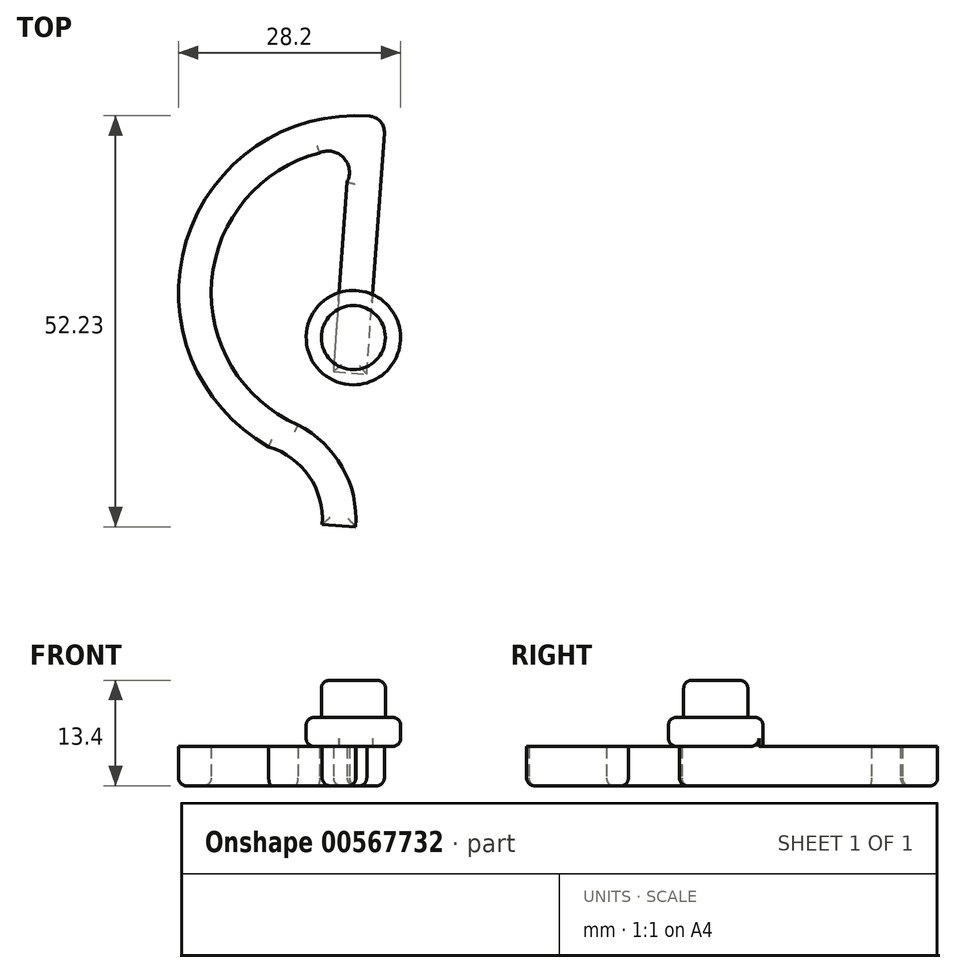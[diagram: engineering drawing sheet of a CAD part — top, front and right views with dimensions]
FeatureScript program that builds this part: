
annotation { "Feature Type Name" : "Feature", "Feature Type Description" : "" }
export const myFeature = defineFeature(function(context is Context, id is Id, definition is map)
    precondition{}
    {
        {
            var Q0;
            Q0=qCreatedBy(makeId("Front.planeOp"),FACE);
            var sketch = newSketch(context, id + "F0", { "sketchPlane" : qUnion([Q0])});
            skEllipticalArc(sketch, "E0", {});
            skArc(sketch, "E1", {"start": v(32.14, -13.74) * mm, "mid": v(46.1, 8.58) * mm, "end": v(25.17, 24.54) * mm});
            skArc(sketch, "E2.filletArc", {"start": v(23.1, 27.15) * mm, "mid": v(23.43, 25.29) * mm, "end": v(25.17, 24.54) * mm});
            skPoint(sketch, "E3.visualSharp", {"position": v(28.3, -14.4) * mm});
            skArc(sketch, "E3.filletArc", {"start": v(32.14, -13.74) * mm, "mid": v(30.7, -15.37) * mm, "end": v(31.6, -17.35) * mm});
            skArc(sketch, "E4", {"start": v(-52.78, 36.46) * mm, "mid": v(-76.5, 19.2) * mm, "end": v(-62.96, -6.82) * mm});
            skLineSegment(sketch, "E5", {"start": v(-55.53, 30.2) * mm, "end": v(-57.43, 4.02) * mm});
            skLineSegment(sketch, "E6", {"start": v(-58.84, -15.39) * mm, "end": v(-54.59, -15.7) * mm});
            skArc(sketch, "E7", {"start": v(-58.18, 32.03) * mm, "mid": v(-72.83, 16.02) * mm, "end": v(-61.94, -2.74) * mm});
            skLineSegment(sketch, "E8", {"start": v(-57.43, 4.02) * mm, "end": v(-53.18, 3.72) * mm});
            skLineSegment(sketch, "E9.trimOffspring", {"start": v(-53.18, 3.72) * mm, "end": v(-50.95, 34.32) * mm});
            skArc(sketch, "E10", {"start": v(-55.68, 28.12) * mm, "mid": v(-56.12, 31.19) * mm, "end": v(-59.16, 31.8) * mm});
            skArc(sketch, "E11", {"start": v(-58.84, -15.39) * mm, "mid": v(-60.5, -9.27) * mm, "end": v(-65.63, -5.54) * mm});
            skArc(sketch, "E12", {"start": v(-54.59, -15.7) * mm, "mid": v(-56.51, -7.74) * mm, "end": v(-62.7, -2.39) * mm});
            skPoint(sketch, "E13.visualSharp", {"position": v(-50.81, 36.21) * mm});
            skArc(sketch, "E13.filletArc", {"start": v(-50.95, 34.32) * mm, "mid": v(-51.43, 35.77) * mm, "end": v(-52.78, 36.46) * mm});
            const initialGuessF0  = {"E0": [0.03683771193027496, 0.011276849545538425, 0, -1, 0.03025954682379961, 0.01614231554877723, 5.952785884912911, 4.160081685940753]};
            skSetInitialGuess(sketch, initialGuessF0);
            skSolve(sketch);
        }
        {
            var Q0;
            {var subQ15=sQuery(id+"F0.wireOp",EDGE,"E6");Q0=makeQuery(id+"F0.imprint","IMPRINT",FACE,{"disambiguationData":[TD([[makeQuery(id+"F0.imprint","IMPRINT",EDGE,{"derivedFrom":subQ15}),1.0]])]});}
            extrude(context, id + "F1", {"entities" : qUnion([Q0]), "depth" : 5 * mm, "offsetDistance" : 25 * mm});
        }
        {
            var Q0;
            Q0=makeQuery(id+"F1.opExtrude","CAP_FACE",FACE,{"disambiguationData":[OSD([sQuery(id+"F0.wireOp",EDGE,"E4"),sQuery(id+"F0.wireOp",EDGE,"E5"),sQuery(id+"F0.wireOp",EDGE,"E6"),sQuery(id+"F0.wireOp",EDGE,"E7"),sQuery(id+"F0.wireOp",EDGE,"E8"),sQuery(id+"F0.wireOp",EDGE,"E9.trimOffspring"),sQuery(id+"F0.wireOp",EDGE,"E10"),sQuery(id+"F0.wireOp",EDGE,"E11"),sQuery(id+"F0.wireOp",EDGE,"E12")])],"isStart":false});
            var sketch = newSketch(context, id + "F2", { "sketchPlane" : qUnion([Q0])});
            skCircle(sketch, "E14", {"center": v(-54.88, 8.34) * mm, "radius": 6 * mm});
            skSolve(sketch);
        }
        {
            var Q0;
            {var subQ5=makeQuery(id+"F1.opExtrude","CAP_EDGE",EDGE,{"disambiguationData":[OSD([sQuery(id+"F0.wireOp",EDGE,"E8")])],"isStart":false});Q0=makeQuery(id+"F2.imprint","IMPRINT",FACE,{"disambiguationData":[TD([[makeQuery(id+"F2.imprint","IMPRINT",EDGE,{"derivedFrom":subQ5}),-1.0]])]});}
            var Q1;
            {var subQ5=makeQuery(id+"F1.opExtrude","CAP_EDGE",EDGE,{"disambiguationData":[OSD([sQuery(id+"F0.wireOp",EDGE,"E8")])],"isStart":false});Q1=makeQuery(id+"F2.imprint","IMPRINT",FACE,{"disambiguationData":[TD([[makeQuery(id+"F2.imprint","IMPRINT",EDGE,{"derivedFrom":subQ5}),1.0]])]});}
            extrude(context, id + "F3", {"entities" : qUnion([Q0, Q1]), "operationType" : NewBodyOperationType.ADD, "depth" : 3.7 * mm, "offsetDistance" : 25 * mm});
        }
        {
            var Q0;
            Q0=makeQuery(id+"F3.opExtrude","CAP_FACE",FACE,{"disambiguationData":[OSD([sQuery(id+"F2.wireOp",EDGE,"E14")])],"isStart":false});
            var sketch = newSketch(context, id + "F4", { "sketchPlane" : qUnion([Q0])});
            skCircle(sketch, "E15", {"center": v(-54.88, 8.34) * mm, "radius": 4.07 * mm});
            skSolve(sketch);
        }
        {
            var Q0;
            Q0=makeQuery(id+"F4.imprint","IMPRINT",FACE,{"disambiguationData":[TD([[makeQuery(id+"F4.imprint","IMPRINT",EDGE,{"derivedFrom":sQuery(id+"F4.wireOp",EDGE,"E15")}),1.0]])]});
            extrude(context, id + "F5", {"entities" : qUnion([Q0]), "operationType" : NewBodyOperationType.ADD, "depth" : 4.7 * mm, "offsetDistance" : 25 * mm});
        }
        {
            var Q0;
            Q0=makeQuery(id+"F5.opExtrude","CAP_EDGE",EDGE,{"disambiguationData":[OSD([sQuery(id+"F4.wireOp",EDGE,"E15")])],"isStart":false});
            fillet(context, id + "F6", {"entities" : qUnion([Q0]), "radius" : 1 * mm, "tangentPropagation" : true, "allowEdgeOverflow" : false});
        }
        {
            var Q0;
            Q0=makeQuery(id+"F3.opExtrude","CAP_EDGE",EDGE,{"disambiguationData":[OSD([sQuery(id+"F2.wireOp",EDGE,"E14")])],"isStart":false});
            var Q1;
            {var subQ0=sQuery(id+"F2.wireOp",EDGE,"E14");Q1=makeQuery(id+"F3.boolean.opBoolean","SPLIT",EDGE,{"disambiguationData":[topologyDisambiguationEdgeConnected([makeQuery(id+"F3.opExtrude","CAP_FACE",FACE,{"disambiguationData":[OSD([subQ0])],"isStart":true})])],"derivedFrom":makeQuery(id+"F3.opExtrude","CAP_EDGE",EDGE,{"disambiguationData":[OSD([subQ0])],"isStart":true})});}
            fillet(context, id + "F7", {"entities" : qUnion([Q0, Q1]), "radius" : 1 * mm, "tangentPropagation" : true, "allowEdgeOverflow" : false});
        }
        {
            var Q0;
            Q0=makeQuery(id+"F1.opExtrude","CAP_FACE",FACE,{"disambiguationData":[OSD([sQuery(id+"F0.wireOp",EDGE,"E4"),sQuery(id+"F0.wireOp",EDGE,"E5"),sQuery(id+"F0.wireOp",EDGE,"E6"),sQuery(id+"F0.wireOp",EDGE,"E7"),sQuery(id+"F0.wireOp",EDGE,"E8"),sQuery(id+"F0.wireOp",EDGE,"E9.trimOffspring"),sQuery(id+"F0.wireOp",EDGE,"E10"),sQuery(id+"F0.wireOp",EDGE,"E11"),sQuery(id+"F0.wireOp",EDGE,"E12")])],"isStart":true});
            fillet(context, id + "F8", {"entities" : qUnion([Q0]), "radius" : 1 * mm, "tangentPropagation" : true, "allowEdgeOverflow" : false});
        }
        {
            var Q0;
            Q0=qCreatedBy(makeId("Top.planeOp"),FACE);
            var sketch = newSketch(context, id + "F9", { "sketchPlane" : qUnion([Q0])});
            skLineSegment(sketch, "E16.bottom", {"start": v(-19.3, -25.63) * mm, "end": v(29.04, -25.63) * mm});
            skLineSegment(sketch, "E16.top", {"start": v(-19.3, 28.73) * mm, "end": v(29.04, 28.73) * mm});
            skLineSegment(sketch, "E16.left", {"start": v(-19.3, -25.63) * mm, "end": v(-19.3, 28.73) * mm});
            skLineSegment(sketch, "E16.right", {"start": v(29.04, -25.63) * mm, "end": v(29.04, 28.73) * mm});
            skSolve(sketch);
        }
        {
            var Q0;
            Q0=makeQuery(id+"F1.opExtrude","SWEPT_BODY",BODY,{"disambiguationData":[OSD([sQuery(id+"F0.wireOp",EDGE,"E4"),sQuery(id+"F0.wireOp",EDGE,"E5"),sQuery(id+"F0.wireOp",EDGE,"E6"),sQuery(id+"F0.wireOp",EDGE,"E7"),sQuery(id+"F0.wireOp",EDGE,"E8"),sQuery(id+"F0.wireOp",EDGE,"E9.trimOffspring"),sQuery(id+"F0.wireOp",EDGE,"E10"),sQuery(id+"F0.wireOp",EDGE,"E11"),sQuery(id+"F0.wireOp",EDGE,"E12"),sQuery(id+"F0.wireOp",EDGE,"E13.filletArc")])]});
            var Q1;
            Q1=sQuery(id+"F9.wireOp",EDGE,"E16.top");
            transform(context, id + "F10", {"entities" : qUnion([Q0]), "transformType" : TransformType.ROTATION, "transformAxis" : qUnion([Q1]), "angle" : 270 * degree, "makeCopy" : false});
        }
        {
            var Q0;
            Q0=makeQuery(id+"F1.opExtrude","SWEPT_BODY",BODY,{"disambiguationData":[OSD([sQuery(id+"F0.wireOp",EDGE,"E4"),sQuery(id+"F0.wireOp",EDGE,"E5"),sQuery(id+"F0.wireOp",EDGE,"E6"),sQuery(id+"F0.wireOp",EDGE,"E7"),sQuery(id+"F0.wireOp",EDGE,"E8"),sQuery(id+"F0.wireOp",EDGE,"E9.trimOffspring"),sQuery(id+"F0.wireOp",EDGE,"E10"),sQuery(id+"F0.wireOp",EDGE,"E11"),sQuery(id+"F0.wireOp",EDGE,"E12"),sQuery(id+"F0.wireOp",EDGE,"E13.filletArc")])]});
            transform(context, id + "F11", {"entities" : qUnion([Q0]), "transformType" : TransformType.TRANSLATION_3D, "dx" : 0 * mm, "dy" : 0 * mm, "dz" : -28.6 * mm, "makeCopy" : false});
        }
    });
